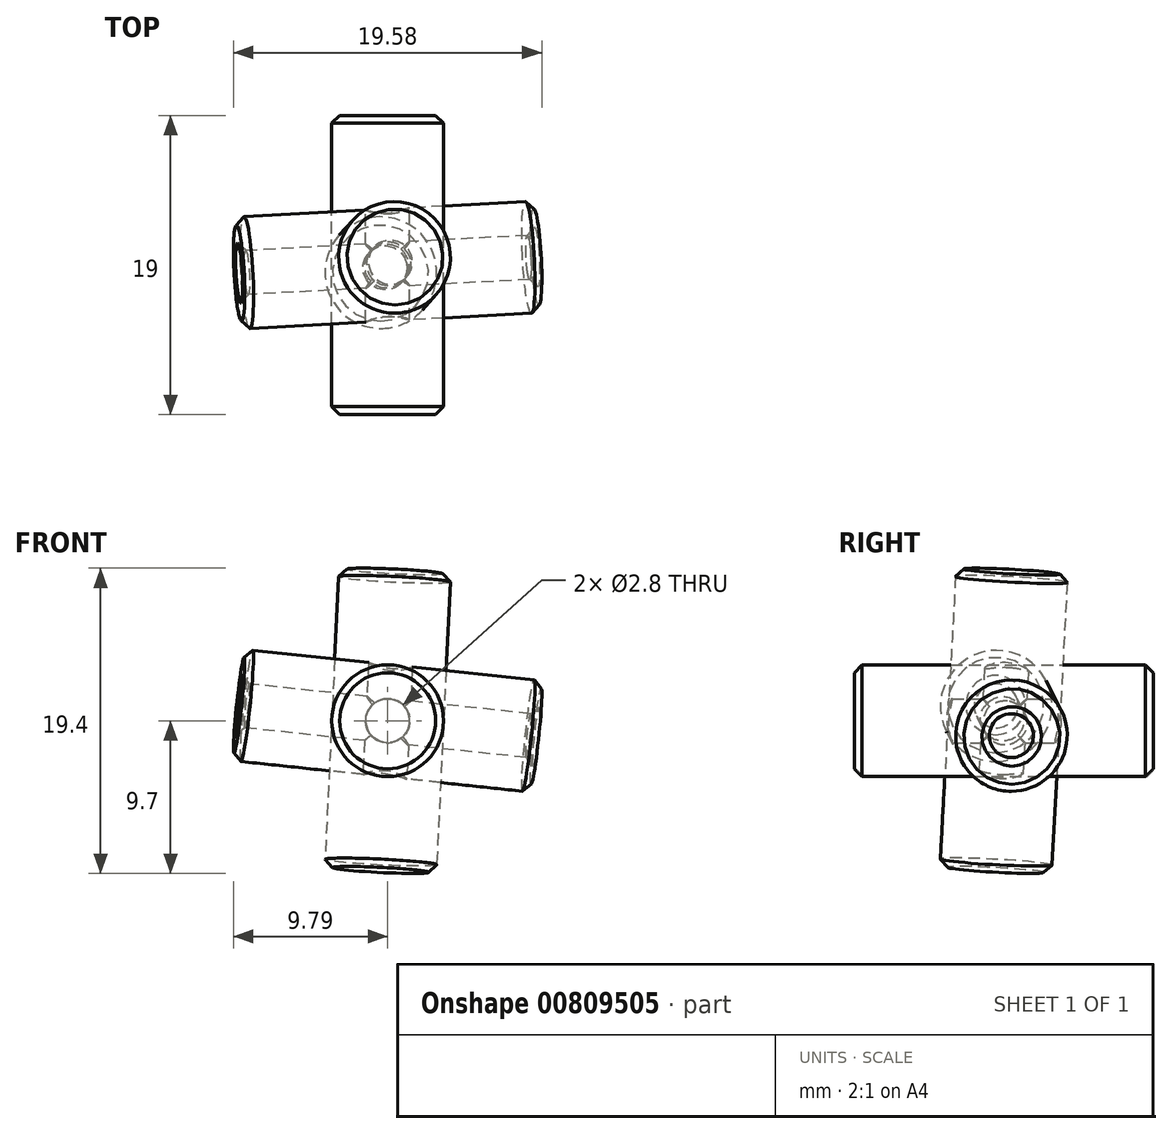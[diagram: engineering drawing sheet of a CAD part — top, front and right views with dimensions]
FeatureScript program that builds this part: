
annotation { "Feature Type Name" : "Feature", "Feature Type Description" : "" }
export const myFeature = defineFeature(function(context is Context, id is Id, definition is map)
    precondition{}
    {
        {
            var Q0;
            Q0=qCreatedBy(makeId("Front.planeOp"),FACE);
            var sketch = newSketch(context, id + "F0", { "sketchPlane" : qUnion([Q0])});
            skCircle(sketch, "E0", {"center": v(0, 0) * mm, "radius": 3.55 * mm});
            skSolve(sketch);
        }
        {
            var Q0;
            Q0=qCreatedBy(makeId("Front.planeOp"),FACE);
            var sketch = newSketch(context, id + "F1", { "sketchPlane" : qUnion([Q0])});
            skCircle(sketch, "E1", {"center": v(0, 0) * mm, "radius": 1.4 * mm});
            skSolve(sketch);
        }
        {
            var Q0;
            Q0 = qSketchRegion(id + "F0", true);
            extrude(context, id + "F2", {"entities" : qUnion([Q0]), "endBound" : BoundingType.SYMMETRIC, "depth" : 19 * mm, "offsetDistance" : 25 * mm});
        }
        {
            var Q0;
            Q0 = qSketchRegion(id + "F1", true);
            extrude(context, id + "F3", {"entities" : qUnion([Q0]), "endBound" : BoundingType.SYMMETRIC, "depth" : 20 * mm, "offsetDistance" : 25 * mm});
        }
        {
            var Q0;
            Q0=qCreatedBy(makeId("Front.planeOp"),FACE);
            var sketch = newSketch(context, id + "F4", { "sketchPlane" : qUnion([Q0])});
            skLineSegment(sketch, "E2.bottom", {"start": v(0, 0) * mm, "end": v(11.67, 0) * mm});
            skLineSegment(sketch, "E2.top", {"start": v(0, 10) * mm, "end": v(11.67, 10) * mm});
            skLineSegment(sketch, "E2.left", {"start": v(0, 0) * mm, "end": v(0, 10) * mm});
            skLineSegment(sketch, "E2.right", {"start": v(11.67, 0) * mm, "end": v(11.67, 10) * mm});
            skSolve(sketch);
        }
        {
            var Q0;
            Q0 = qSketchRegion(id + "F4", true);
            extrude(context, id + "F5", {"entities" : qUnion([Q0]), "depth" : 10 * mm, "offsetDistance" : 25 * mm});
        }
        {
            var Q0;
            Q0=qCreatedBy(makeId("Origin.pointOp"),VERTEX);
            var Q1;
            Q1=makeQuery(id+"F5.opExtrude","CAP_VERTEX",VERTEX,{"disambiguationData":[OSD([sQuery(id+"F4.wireOp",EDGE,"E2.top"),sQuery(id+"F4.wireOp",EDGE,"E2.right")])],"isStart":false});
            var Q2;
            Q2=makeQuery(id+"F5.opExtrude","CAP_VERTEX",VERTEX,{"disambiguationData":[OSD([sQuery(id+"F4.wireOp",EDGE,"E2.bottom"),sQuery(id+"F4.wireOp",EDGE,"E2.right")])],"isStart":false});
            cPlane(context, id + "F6", {"entities" : qUnion([Q0, Q1, Q2]), "cplaneType" : CPlaneType.THREE_POINT, "offset" : 25 * mm, "width" : 150 * mm, "height" : 150 * mm});
        }
        {
            var Q0;
            Q0=qCreatedBy(id+"F6.planeOp",FACE);
            var sketch = newSketch(context, id + "F7", { "sketchPlane" : qUnion([Q0])});
            skLineSegment(sketch, "E3", {"start": v(0, 0) * mm, "end": v(15.37, 10) * mm});
            skSolve(sketch);
        }
        {
            var Q0;
            Q0=makeQuery(id+"F5.opExtrude","SWEPT_BODY",BODY,{"disambiguationData":[OSD([sQuery(id+"F4.wireOp",EDGE,"E2.bottom"),sQuery(id+"F4.wireOp",EDGE,"E2.top"),sQuery(id+"F4.wireOp",EDGE,"E2.left"),sQuery(id+"F4.wireOp",EDGE,"E2.right")])]});
            deleteBodies(context, id + "F8", {"entities" : qUnion([Q0])});
        }
        {
            var Q0;
            Q0=makeQuery(id+"F2.opExtrude","SWEPT_BODY",BODY,{"disambiguationData":[OSD([sQuery(id+"F0.wireOp",EDGE,"E0")])]});
            var Q1;
            Q1=makeQuery(id+"F3.opExtrude","SWEPT_BODY",BODY,{"disambiguationData":[OSD([sQuery(id+"F1.wireOp",EDGE,"E1")])]});
            var Q2;
            Q2=sQuery(id+"F7.wireOp",EDGE,"E3");
            circularPattern(context, id + "F9", {"entities" : qUnion([Q0, Q1]), "axis" : qUnion([Q2]), "angle" : 360 * degree, "instanceCount" : 3, "equalSpace" : true});
        }
        {
            var Q0;
            Q0=makeQuery(id+"F9.opPattern","COPY",BODY,{"derivedFrom":makeQuery(id+"F3.opExtrude","SWEPT_BODY",BODY,{"disambiguationData":[OSD([sQuery(id+"F1.wireOp",EDGE,"E1")])]}),"instanceName":"2"});
            var Q1;
            Q1=makeQuery(id+"F3.opExtrude","SWEPT_BODY",BODY,{"disambiguationData":[OSD([sQuery(id+"F1.wireOp",EDGE,"E1")])]});
            var Q2;
            Q2=makeQuery(id+"F9.opPattern","COPY",BODY,{"derivedFrom":makeQuery(id+"F3.opExtrude","SWEPT_BODY",BODY,{"disambiguationData":[OSD([sQuery(id+"F1.wireOp",EDGE,"E1")])]}),"instanceName":"1"});
            var Q3;
            Q3=makeQuery(id+"F9.opPattern","COPY",BODY,{"derivedFrom":makeQuery(id+"F2.opExtrude","SWEPT_BODY",BODY,{"disambiguationData":[OSD([sQuery(id+"F0.wireOp",EDGE,"E0")])]}),"instanceName":"1"});
            booleanBodies(context, id + "F10", {"operationType" : BooleanOperationType.SUBTRACTION, "tools" : qUnion([Q0, Q1, Q2]), "targets" : qUnion([Q3])});
        }
        {
            var Q0;
            Q0=makeQuery(id+"F2.opExtrude","CAP_FACE",FACE,{"disambiguationData":[OSD([sQuery(id+"F0.wireOp",EDGE,"E0")])],"isStart":true});
            var Q1;
            Q1=makeQuery(id+"F9.opPattern","COPY",FACE,{"derivedFrom":makeQuery(id+"F2.opExtrude","CAP_FACE",FACE,{"disambiguationData":[OSD([sQuery(id+"F0.wireOp",EDGE,"E0")])],"isStart":false}),"instanceName":"2"});
            var Q2;
            Q2=makeQuery(id+"F2.opExtrude","CAP_FACE",FACE,{"disambiguationData":[OSD([sQuery(id+"F0.wireOp",EDGE,"E0")])],"isStart":false});
            var Q3;
            Q3=makeQuery(id+"F9.opPattern","COPY",FACE,{"derivedFrom":makeQuery(id+"F2.opExtrude","CAP_FACE",FACE,{"disambiguationData":[OSD([sQuery(id+"F0.wireOp",EDGE,"E0")])],"isStart":true}),"instanceName":"2"});
            var Q4;
            Q4=makeQuery(id+"F9.opPattern","COPY",FACE,{"derivedFrom":makeQuery(id+"F2.opExtrude","CAP_FACE",FACE,{"disambiguationData":[OSD([sQuery(id+"F0.wireOp",EDGE,"E0")])],"isStart":false}),"instanceName":"1"});
            var Q5;
            Q5=makeQuery(id+"F9.opPattern","COPY",FACE,{"derivedFrom":makeQuery(id+"F2.opExtrude","CAP_FACE",FACE,{"disambiguationData":[OSD([sQuery(id+"F0.wireOp",EDGE,"E0")])],"isStart":true}),"instanceName":"1"});
            chamfer(context, id + "F11", {"entities" : qUnion([Q0, Q1, Q2, Q3, Q4, Q5]), "width" : 0.5 * mm, "tangentPropagation" : true});
        }
    });
